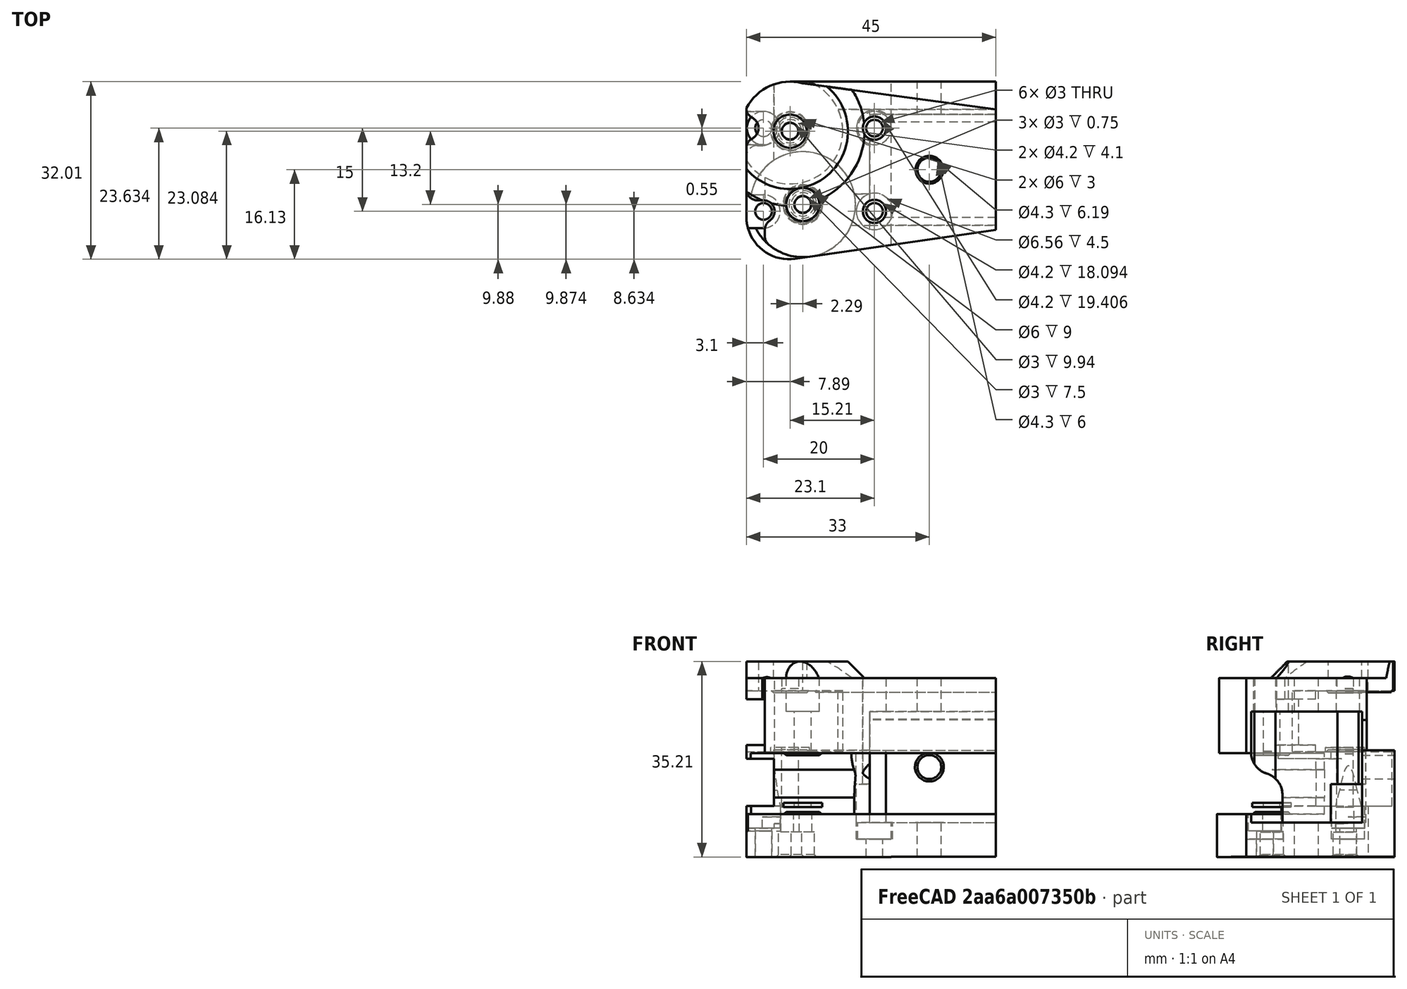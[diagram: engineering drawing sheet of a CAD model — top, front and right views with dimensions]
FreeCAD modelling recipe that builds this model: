
FCSTD DOCUMENT  (FreeCAD 0.18R16146 (Git))
Label: carrier-CF-left
License: All rights reserved
LicenseURL: http://en.wikipedia.org/wiki/All_rights_reserved
objects: Part::Cylinder×20, Part::Cut×13, Part::MultiFuse×9, Part::Feature×5, Part::Chamfer×5, Part::Box×3
note: 55 computed .brp shape members not serialized (recipe doc carries the construction recipe); baked Part::Feature solids carry a one-line shape summary decoded from their .brp

FEATURE [Part::Box] Box  label="Cube"
  AttacherType = Attacher::AttachEngine3D
  Height = 20
  Length = 70
  Placement = pos=(2.13,-5.55,16.2) rot=(0,0,1;0rad)
  Width = 20
FEATURE [Part::Cylinder] Cylinder
  Angle = 360
  AttacherType = Attacher::AttachEngine3D
  Height = 6
  Placement = pos=(12.9,4.45,36.2) rot=(0,0,1;0rad)
  Radius = 2.6
FEATURE [Part::Cylinder] Cylinder001
  Angle = 360
  AttacherType = Attacher::AttachEngine3D
  Height = 14.2
  Placement = pos=(12.9,4.45,2) rot=(0,0,1;0rad)
  Radius = 2.6
FEATURE [Part::Cylinder] Cylinder002
  Angle = 360
  AttacherType = Attacher::AttachEngine3D
  Height = 14.2
  Placement = pos=(12.9,4.45,2) rot=(0,0,1;0rad)
  Radius = 2.15
FEATURE [Part::Cylinder] Cylinder003
  Angle = 360
  AttacherType = Attacher::AttachEngine3D
  Height = 6
  Placement = pos=(12.9,4.45,36.2) rot=(0,0,1;0rad)
  Radius = 2.15
FEATURE [Part::Cylinder] Cylinder004
  Angle = 360
  AttacherType = Attacher::AttachEngine3D
  Height = 5.88
  Placement = pos=(12.9,14.45,26.2) rot=(-1,0,0;1.5708rad)
  Radius = 2.6
FEATURE [Part::Cylinder] Cylinder005
  Angle = 360
  AttacherType = Attacher::AttachEngine3D
  Height = 5.88
  Placement = pos=(12.9,14.45,26.2) rot=(-1,0,0;1.5708rad)
  Radius = 2.15
FEATURE [Part::Cut] Cut004
  Base = -> Cylinder
  Tool = -> Cylinder003
FEATURE [Part::Cut] Cut005
  Base = -> Cylinder001
  Tool = -> Cylinder002
FEATURE [Part::Cut] Cut006
  Base = -> Cylinder004
  Tool = -> Cylinder005
FEATURE [Part::MultiFuse] Fusion002  label="bolt-adapter"
  Shapes = -> [Cut004,Cut006,Cut005]
FEATURE [Part::Feature] Part__Feature142  label="std-left"
  Placement = pos=(8,-213,-461.82) rot=(1,0,0;1.5708rad)
  shape: bbox 47.27 x 33.44 x 45.2 mm, 159 faces (baked)
FEATURE [Part::Cut] Cut
  Base = -> Part__Feature142
  Tool = -> Box
FEATURE [Part::Cylinder] Cylinder006
  Angle = 360
  AttacherType = Attacher::AttachEngine3D
  Height = 11
  Placement = pos=(-12.21,11.4,28.95) rot=(0,0,1;0rad)
  Radius = 9.5
FEATURE [Part::Cylinder] Cylinder007
  Angle = 360
  AttacherType = Attacher::AttachEngine3D
  Height = 0.75
  Placement = pos=(-12.21,11.4,28.95) rot=(0,0,1;0rad)
  Radius = 3.5
FEATURE [Part::Cylinder] Cylinder008
  Angle = 360
  AttacherType = Attacher::AttachEngine3D
  Height = 0.75
  Placement = pos=(-12.21,11.4,28.95) rot=(0,0,1;0rad)
  Radius = 1.5
FEATURE [Part::Cylinder] Cylinder009
  Angle = 360
  AttacherType = Attacher::AttachEngine3D
  Height = 0.75
  Placement = pos=(-9.92,-1.8,19) rot=(0,0,1;0rad)
  Radius = 3.5
FEATURE [Part::Cylinder] Cylinder010
  Angle = 360
  AttacherType = Attacher::AttachEngine3D
  Height = 3
  Placement = pos=(-9.92,-1.8,25.7) rot=(0,0,1;0rad)
  Radius = 9.5
FEATURE [Part::Cylinder] Cylinder011
  Angle = 360
  AttacherType = Attacher::AttachEngine3D
  Height = 3
  Placement = pos=(-9.92,-1.8,17.7) rot=(0,0,1;0rad)
  Radius = 9.5
FEATURE [Part::Cylinder] Cylinder012
  Angle = 360
  AttacherType = Attacher::AttachEngine3D
  Height = 0.75
  Placement = pos=(-9.92,-1.8,19) rot=(0,0,1;0rad)
  Radius = 1.5
FEATURE [Part::Cut] Cut008002005
  Base = -> Cylinder007
  Tool = -> Cylinder008
FEATURE [Part::Feature] Cut008002005001  label="Cut008002006"
  Placement = pos=(0,0,10.6) rot=(0,0,1;0rad)
  shape: bbox 7 x 7 x 0.75 mm, 4 faces (baked)
FEATURE [Part::Feature] Cut008002005003  label="Cut008002009"
  Placement = pos=(0,0,-0.35) rot=(0,0,1;0rad)
  shape: bbox 7 x 7 x 0.75 mm, 4 faces (baked)
FEATURE [Part::Chamfer] Chamfer002
  Base = -> Cut008002005001
  Edges = 1 edges r=0.5: [Edge3]
FEATURE [Part::Chamfer] Chamfer003
  Base = -> Cut008002005003
  Edges = 1 edges r=0.5: [Edge1]
FEATURE [Part::Cut] Cut008002005004
  Base = -> Cylinder009
  Tool = -> Cylinder012
FEATURE [Part::Feature] Cut008002005004001  label="Cut008002005005"
  Placement = pos=(0,0,9.3) rot=(0,0,1;0rad)
  shape: bbox 7 x 7 x 0.75 mm, 4 faces (baked)
FEATURE [Part::Feature] Cut008002005004002  label="Cut008002005006"
  Placement = pos=(0,0,-1.65) rot=(0,0,1;0rad)
  shape: bbox 7 x 7 x 0.75 mm, 4 faces (baked)
FEATURE [Part::Chamfer] Chamfer004
  Base = -> Cut008002005004001
  Edges = 1 edges r=0.5: [Edge3]
FEATURE [Part::Chamfer] Chamfer005
  Base = -> Cut008002005004002
  Edges = 1 edges r=0.5: [Edge1]
FEATURE [Part::Box] Box007  label="Cube007"
  AttacherType = Attacher::AttachEngine3D
  Height = 10
  Length = 10
  Placement = pos=(-25.1,5.95,21.7) rot=(0,0,1;0rad)
  Width = 10
FEATURE [Part::Cut] Cut008002005004003
  Base = -> Chamfer003
  Tool = -> Box007
FEATURE [Part::MultiFuse] Fusion005
  Shapes = -> [Cut008002005004003,Chamfer005,Chamfer004,Chamfer002]
FEATURE [Part::Cylinder] Cylinder013
  Angle = 360
  AttacherType = Attacher::AttachEngine3D
  Height = 6
  Placement = pos=(-9.92,-1.8,10) rot=(0,0,1;0rad)
  Radius = 3.3
FEATURE [Part::Cylinder] Cylinder014
  Angle = 360
  AttacherType = Attacher::AttachEngine3D
  Height = 6
  Placement = pos=(-12.21,11.4,10.01) rot=(0,0,1;0rad)
  Radius = 3.3
FEATURE [Part::Cylinder] Cylinder015
  Angle = 360
  AttacherType = Attacher::AttachEngine3D
  Height = 4.5
  Placement = pos=(-12.21,11.4,10.01) rot=(0,0,1;0rad)
  Radius = 2.1
FEATURE [Part::Cylinder] Cylinder016
  Angle = 360
  AttacherType = Attacher::AttachEngine3D
  Height = 4.5
  Placement = pos=(-9.92,-1.8,10) rot=(0,0,1;0rad)
  Radius = 2.1
FEATURE [Part::Cylinder] Cylinder017
  Angle = 360
  AttacherType = Attacher::AttachEngine3D
  Height = 2
  Placement = pos=(-17,11.96,15.2) rot=(0,0,1;0rad)
  Radius = 3
FEATURE [Part::MultiFuse] Fusion009
  Shapes = -> [Cylinder013,Cylinder014]
FEATURE [Part::MultiFuse] Fusion
  Shapes = -> [Fusion002,Cut]
FEATURE [Part::Cut] Cut008002005004004
  Base = -> Fusion
  Tool = -> Cylinder006
FEATURE [Part::Cut] Cut008002005004005
  Base = -> Cut008002005004004
  Tool = -> Cylinder011
FEATURE [Part::Cut] Cut008002005004006
  Base = -> Cut008002005004005
  Tool = -> Cylinder010
FEATURE [Part::MultiFuse] Fusion010
  Shapes = -> [Fusion005,Cut008002005004006]
FEATURE [Part::MultiFuse] Fusion011
  Shapes = -> [Fusion009,Fusion010]
FEATURE [Part::Cylinder] Cylinder018
  Angle = 360
  AttacherType = Attacher::AttachEngine3D
  Height = 9
  Placement = pos=(-9.92,-1.8,10) rot=(0,0,1;0rad)
  Radius = 1.65
FEATURE [Part::Cylinder] Cylinder019
  Angle = 360
  AttacherType = Attacher::AttachEngine3D
  Height = 9
  Placement = pos=(-12.21,11.4,10.01) rot=(0,0,1;0rad)
  Radius = 1.65
FEATURE [Part::MultiFuse] Fusion012
  Shapes = -> [Cylinder016,Cylinder015]
FEATURE [Part::MultiFuse] Fusion013
  Shapes = -> [Cylinder019,Cylinder018]
FEATURE [Part::MultiFuse] Fusion014
  Shapes = -> [Fusion013,Fusion012]
FEATURE [Part::Cut] Cut008002005004007
  Base = -> Fusion011
  Tool = -> Fusion014
FEATURE [Part::Cut] Cut008002005004008
  Base = -> Cut008002005004007
  Tool = -> Cylinder017
FEATURE [Part::Box] Box008  label="Cube008"
  AttacherType = Attacher::AttachEngine3D
  Height = 15
  Length = 23
  Placement = pos=(6,-18,-4.99) rot=(0,0,1;0rad)
  Width = 42
FEATURE [Part::Cut] Cut008002005004009
  Base = -> Cut008002005004008
  Tool = -> Box008
FEATURE [Part::Chamfer] Chamfer
  Base = -> Cut008002005004009
  Edges = 2 edges r=0.4: [Edge21,Edge160]
